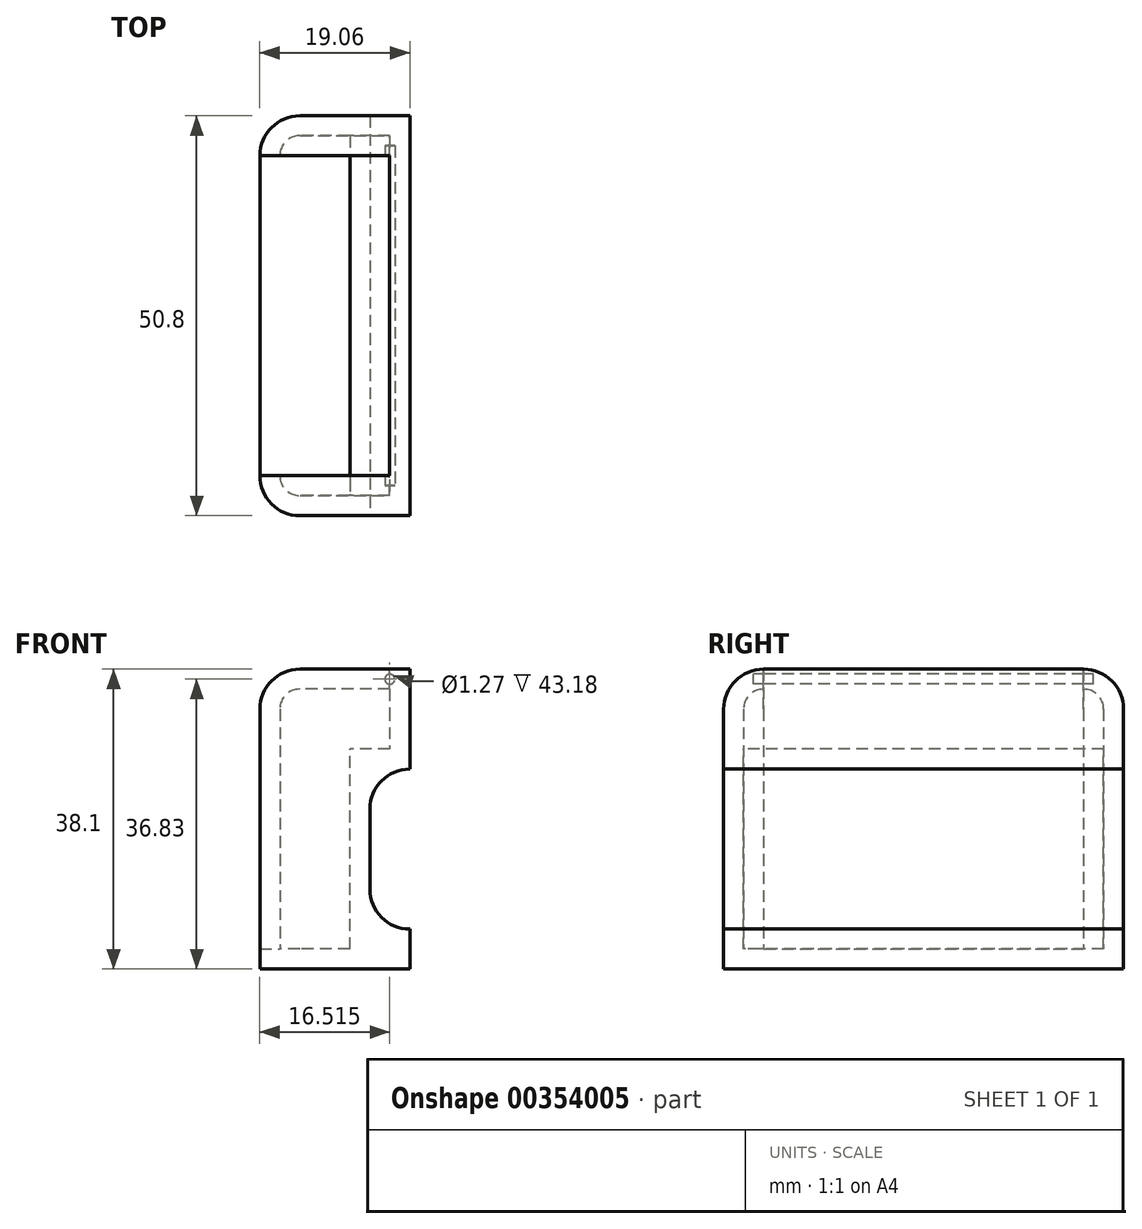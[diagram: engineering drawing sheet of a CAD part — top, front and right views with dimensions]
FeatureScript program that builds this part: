
annotation { "Feature Type Name" : "Feature", "Feature Type Description" : "" }
export const myFeature = defineFeature(function(context is Context, id is Id, definition is map)
    precondition{}
    {
        {
            var Q0;
            Q0=qCreatedBy(makeId("Top.planeOp"),FACE);
            var sketch = newSketch(context, id + "F0", { "sketchPlane" : qUnion([Q0])});
            skLineSegment(sketch, "E0.bottom", {"start": v(9.53, -25.4) * mm, "end": v(-9.52, -25.4) * mm});
            skLineSegment(sketch, "E0.top", {"start": v(9.52, 25.4) * mm, "end": v(-9.53, 25.4) * mm});
            skLineSegment(sketch, "E0.left", {"start": v(9.53, -25.4) * mm, "end": v(9.52, 25.4) * mm});
            skLineSegment(sketch, "E0.right", {"start": v(-9.52, -25.4) * mm, "end": v(-9.53, 25.4) * mm});
            skPoint(sketch, "E0.middle", {"position": v(0, 0) * mm});
            skSolve(sketch);
        }
        {
            var Q0;
            Q0=makeQuery(id+"F0.imprint","IMPRINT",FACE,{"disambiguationData":[TD([[makeQuery(id+"F0.imprint","IMPRINT",EDGE,{"derivedFrom":sQuery(id+"F0.wireOp",EDGE,"E0.bottom")}),-1.0]])]});
            extrude(context, id + "F1", {"entities" : qUnion([Q0]), "depth" : 38.1 * mm});
        }
        {
            var Q0;
            Q0=makeQuery(id+"F1.opExtrude","CAP_EDGE",EDGE,{"disambiguationData":[OSD([sQuery(id+"F0.wireOp",EDGE,"E0.bottom")])],"isStart":false});
            var Q1;
            Q1=makeQuery(id+"F1.opExtrude","CAP_EDGE",EDGE,{"disambiguationData":[OSD([sQuery(id+"F0.wireOp",EDGE,"E0.top")])],"isStart":false});
            var Q2;
            Q2=makeQuery(id+"F1.opExtrude","SWEPT_EDGE",EDGE,{"disambiguationData":[OSD([sQuery(id+"F0.wireOp",EDGE,"E0.bottom"),sQuery(id+"F0.wireOp",EDGE,"E0.right")])]});
            var Q3;
            Q3=makeQuery(id+"F1.opExtrude","CAP_EDGE",EDGE,{"disambiguationData":[OSD([sQuery(id+"F0.wireOp",EDGE,"E0.right")])],"isStart":false});
            var Q4;
            Q4=makeQuery(id+"F1.opExtrude","SWEPT_EDGE",EDGE,{"disambiguationData":[OSD([sQuery(id+"F0.wireOp",EDGE,"E0.top"),sQuery(id+"F0.wireOp",EDGE,"E0.right")])]});
            fillet(context, id + "F2", {"entities" : qUnion([Q0, Q1, Q2, Q3, Q4]), "radius" : 5.08 * mm, "tangentPropagation" : true, "allowEdgeOverflow" : false});
        }
        {
            var Q0;
            Q0=makeQuery(id+"F1.opExtrude","SWEPT_FACE",FACE,{"disambiguationData":[OSD([sQuery(id+"F0.wireOp",EDGE,"E0.bottom")])]});
            var sketch = newSketch(context, id + "F3", { "sketchPlane" : qUnion([Q0])});
            skLineSegment(sketch, "E1.bottom", {"start": v(9.53, 5.08) * mm, "end": v(4.45, 5.08) * mm});
            skLineSegment(sketch, "E1.top", {"start": v(9.52, 25.4) * mm, "end": v(4.44, 25.4) * mm});
            skLineSegment(sketch, "E1.left", {"start": v(9.53, 5.08) * mm, "end": v(9.52, 25.4) * mm});
            skLineSegment(sketch, "E1.right", {"start": v(4.45, 5.08) * mm, "end": v(4.44, 25.4) * mm});
            skSolve(sketch);
        }
        {
            var Q0;
            Q0 = qSketchRegion(id + "F3", true);
            extrude(context, id + "F4", {"entities" : qUnion([Q0]), "operationType" : NewBodyOperationType.REMOVE, "oppositeDirection" : true, "depth" : 50.8 * mm});
        }
        {
            var Q0;
            Q0=makeQuery(id+"F1.opExtrude","SWEPT_FACE",FACE,{"disambiguationData":[OSD([sQuery(id+"F0.wireOp",EDGE,"E0.right")])]});
            var Q1;
            Q1=makeQuery(id+"F1.opExtrude","CAP_FACE",FACE,{"disambiguationData":[OSD([sQuery(id+"F0.wireOp",EDGE,"E0.bottom"),sQuery(id+"F0.wireOp",EDGE,"E0.top"),sQuery(id+"F0.wireOp",EDGE,"E0.left"),sQuery(id+"F0.wireOp",EDGE,"E0.right")])],"isStart":false});
            var Q2;
            Q2=makeQuery(id+"F2.opFillet","BLEND_FACE",FACE,{"disambiguationData":[OSD([sQuery(id+"F0.wireOp",EDGE,"E0.right")])]});
            shell(context, id + "F5", {"entities" : qUnion([Q0, Q1, Q2]), "thickness" : 2.54 * mm});
        }
        {
            var Q0;
            Q0=makeQuery(id+"F4.boolean.opBoolean","COPY",EDGE,{"derivedFrom":makeQuery(id+"F4.opExtrude","SWEPT_EDGE",EDGE,{"disambiguationData":[OSD([sQuery(id+"F3.wireOp",EDGE,"E1.bottom"),sQuery(id+"F3.wireOp",EDGE,"E1.right")])]})});
            var Q1;
            Q1=makeQuery(id+"F4.boolean.opBoolean","COPY",EDGE,{"derivedFrom":makeQuery(id+"F4.opExtrude","SWEPT_EDGE",EDGE,{"disambiguationData":[OSD([sQuery(id+"F3.wireOp",EDGE,"E1.top"),sQuery(id+"F3.wireOp",EDGE,"E1.right")])]})});
            fillet(context, id + "F6", {"entities" : qUnion([Q0, Q1]), "radius" : 5.08 * mm, "tangentPropagation" : true, "allowEdgeOverflow" : false});
        }
        {
            var Q0;
            Q0=qCreatedBy(makeId("Front.planeOp"),FACE);
            var sketch = newSketch(context, id + "F7", { "sketchPlane" : qUnion([Q0])});
            skCircle(sketch, "E2", {"center": v(6.99, 36.83) * mm, "radius": 0.64 * mm});
            skSolve(sketch);
        }
        {
            var Q0;
            Q0 = qSketchRegion(id + "F7", true);
            extrude(context, id + "F8", {"entities" : qUnion([Q0]), "operationType" : NewBodyOperationType.REMOVE, "oppositeDirection" : true, "depth" : 43.18 * mm, "symmetric" : true});
        }
    });
